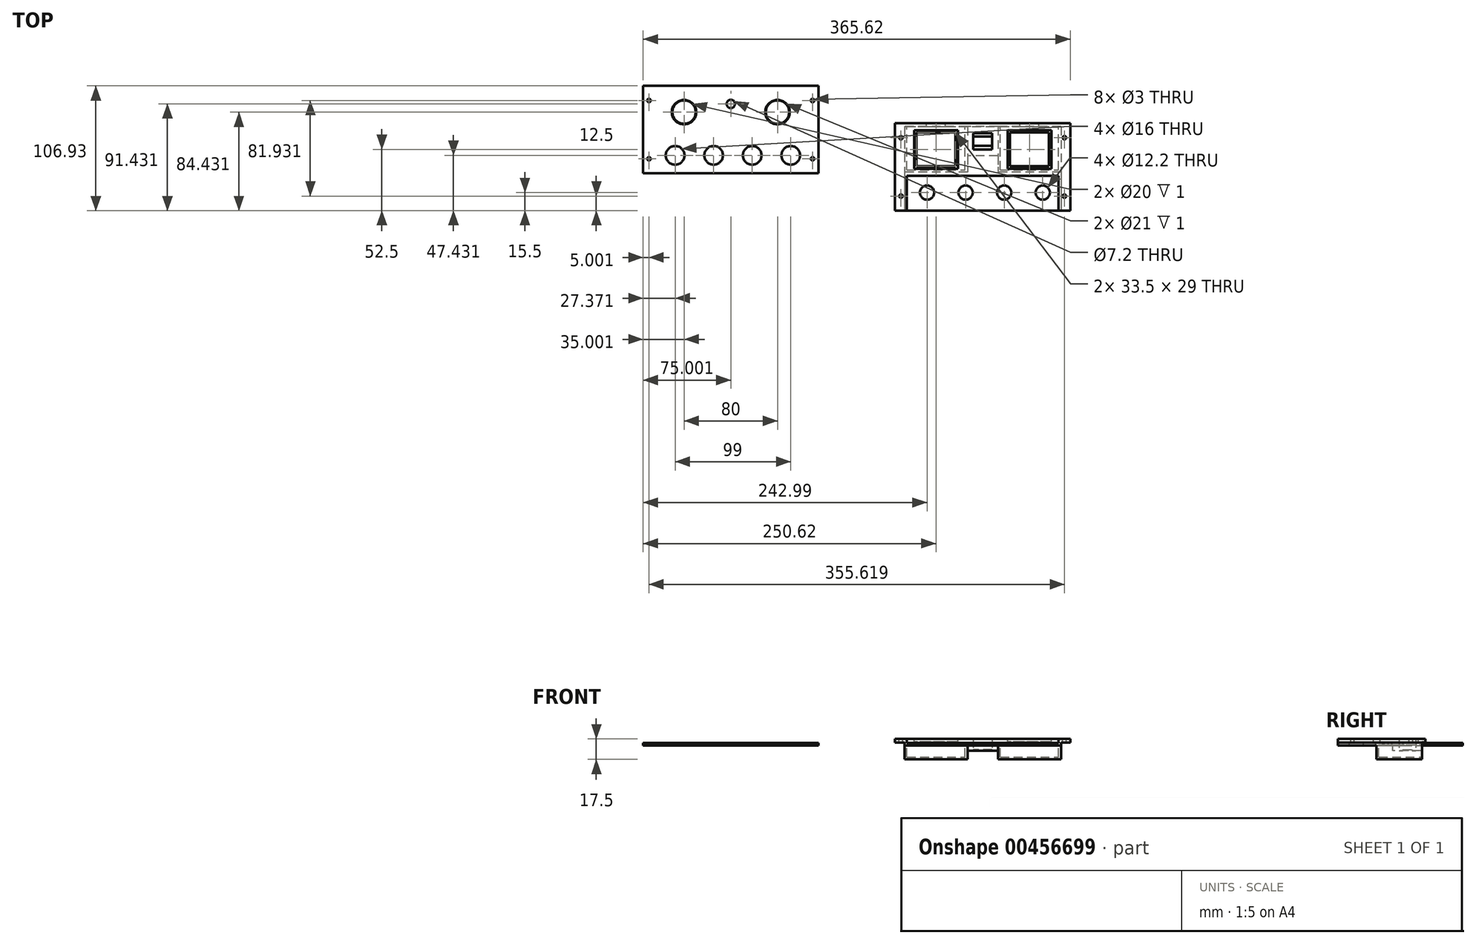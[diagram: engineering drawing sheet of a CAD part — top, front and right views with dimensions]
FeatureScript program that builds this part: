
annotation { "Feature Type Name" : "Feature", "Feature Type Description" : "" }
export const myFeature = defineFeature(function(context is Context, id is Id, definition is map)
    precondition{}
    {
        {
            var Q0;
            Q0=qCreatedBy(makeId("Top.planeOp"),FACE);
            var sketch = newSketch(context, id + "F0", { "sketchPlane" : qUnion([Q0])});
            skLineSegment(sketch, "E0.bottom", {"start": v(75, -37.5) * mm, "end": v(-75, -37.5) * mm});
            skLineSegment(sketch, "E0.top", {"start": v(75, 37.5) * mm, "end": v(-75, 37.5) * mm});
            skLineSegment(sketch, "E0.left", {"start": v(75, -37.5) * mm, "end": v(75, 37.5) * mm});
            skLineSegment(sketch, "E0.right", {"start": v(-75, -37.5) * mm, "end": v(-75, 37.5) * mm});
            skPoint(sketch, "E0.middle", {"position": v(0, 0) * mm});
            skCircle(sketch, "E1", {"center": v(0, 22) * mm, "radius": 5 * mm, "construction": true});
            skCircle(sketch, "E2", {"center": v(-47.63, -22) * mm, "radius": 6.1 * mm});
            skCircle(sketch, "E3.1.0.0", {"center": v(-14.63, -22) * mm, "radius": 6.1 * mm});
            skCircle(sketch, "E3.2.0.0", {"center": v(18.37, -22) * mm, "radius": 6.1 * mm});
            skCircle(sketch, "E3.3.0.0", {"center": v(51.37, -22) * mm, "radius": 6.1 * mm});
            skLineSegment(sketch, "E3.direction1", {"start": v(-47.63, -22) * mm, "end": v(-14.63, -22) * mm, "construction": true});
            skLineSegment(sketch, "E4.bottom", {"start": v(-75, 37.5) * mm, "end": v(-65, 37.5) * mm, "construction": true});
            skLineSegment(sketch, "E4.top", {"start": v(-75, -37.5) * mm, "end": v(-65, -37.5) * mm, "construction": true});
            skLineSegment(sketch, "E4.left", {"start": v(-75, 37.5) * mm, "end": v(-75, -37.5) * mm, "construction": true});
            skLineSegment(sketch, "E4.right", {"start": v(-65, 37.5) * mm, "end": v(-65, -37.5) * mm, "construction": true});
            skLineSegment(sketch, "E5.bottom", {"start": v(75, 37.5) * mm, "end": v(65, 37.5) * mm, "construction": true});
            skLineSegment(sketch, "E5.top", {"start": v(75, -37.5) * mm, "end": v(65, -37.5) * mm, "construction": true});
            skLineSegment(sketch, "E5.left", {"start": v(75, 37.5) * mm, "end": v(75, -37.5) * mm, "construction": true});
            skLineSegment(sketch, "E5.right", {"start": v(65, 37.5) * mm, "end": v(65, -37.5) * mm, "construction": true});
            skPoint(sketch, "E6.middle", {"position": v(-40, 15) * mm});
            skLineSegment(sketch, "E7.bottom", {"start": v(-23.25, 0.5) * mm, "end": v(-56.75, 0.5) * mm});
            skLineSegment(sketch, "E7.top", {"start": v(-23.25, 29.5) * mm, "end": v(-56.75, 29.5) * mm});
            skLineSegment(sketch, "E7.left", {"start": v(-23.25, 0.5) * mm, "end": v(-23.25, 29.5) * mm});
            skLineSegment(sketch, "E7.right", {"start": v(-56.75, 0.5) * mm, "end": v(-56.75, 29.5) * mm});
            skLineSegment(sketch, "E8.bottom", {"start": v(56.75, 0.5) * mm, "end": v(23.25, 0.5) * mm});
            skLineSegment(sketch, "E8.top", {"start": v(56.75, 29.5) * mm, "end": v(23.25, 29.5) * mm});
            skLineSegment(sketch, "E8.left", {"start": v(56.75, 0.5) * mm, "end": v(56.75, 29.5) * mm});
            skLineSegment(sketch, "E8.right", {"start": v(23.25, 0.5) * mm, "end": v(23.25, 29.5) * mm});
            skPoint(sketch, "E8.middle", {"position": v(40, 15) * mm});
            skPoint(sketch, "E9.centerSnap0", {"position": v(-70, 37.5) * mm});
            skCircle(sketch, "E10", {"center": v(-70, 25) * mm, "radius": 1.5 * mm});
            skCircle(sketch, "E11", {"center": v(-70, -25) * mm, "radius": 1.5 * mm});
            skCircle(sketch, "E12", {"center": v(70, 25) * mm, "radius": 1.5 * mm});
            skCircle(sketch, "E13", {"center": v(70, -25) * mm, "radius": 1.5 * mm});
            skLineSegment(sketch, "E14.bottom", {"start": v(8, 15) * mm, "end": v(-8, 15) * mm});
            skLineSegment(sketch, "E14.top", {"start": v(8, 29) * mm, "end": v(-8, 29) * mm});
            skLineSegment(sketch, "E14.left", {"start": v(8, 15) * mm, "end": v(8, 29) * mm});
            skLineSegment(sketch, "E14.right", {"start": v(-8, 15) * mm, "end": v(-8, 29) * mm});
            skLineSegment(sketch, "E15.bottom", {"start": v(8, 18) * mm, "end": v(-8, 18) * mm});
            skLineSegment(sketch, "E15.top", {"start": v(8, 26) * mm, "end": v(-8, 26) * mm});
            skLineSegment(sketch, "E15.left", {"start": v(8, 18) * mm, "end": v(8, 26) * mm});
            skLineSegment(sketch, "E15.right", {"start": v(-8, 18) * mm, "end": v(-8, 26) * mm});
            skSolve(sketch);
        }
        {
            var Q0;
            Q0=makeQuery(id+"F0.imprint","IMPRINT",FACE,{"disambiguationData":[TD([[makeQuery(id+"F0.imprint","IMPRINT",EDGE,{"derivedFrom":sQuery(id+"F0.wireOp",EDGE,"E0.bottom")}),-1.0]])]});
            var Q1;
            Q1=makeQuery(id+"F0.imprint","IMPRINT",FACE,{"disambiguationData":[TD([[makeQuery(id+"F0.imprint","IMPRINT",EDGE,{"derivedFrom":sQuery(id+"F0.wireOp",EDGE,"drD5jItb-HEpr-sxaA-TqkW-DfUxLCmm6Exs")}),-1.0]])]});
            var Q2;
            Q2=makeQuery(id+"F0.imprint","IMPRINT",FACE,{"disambiguationData":[TD([[makeQuery(id+"F0.imprint","IMPRINT",EDGE,{"derivedFrom":sQuery(id+"F0.wireOp",EDGE,"E15.bottom")}),-1.0]])]});
            extrude(context, id + "F1", {"entities" : qUnion([Q0, Q1, Q2]), "depth" : 2 * mm});
        }
        {
            var Q0;
            Q0=makeQuery(id+"F1.opExtrude","CAP_FACE",FACE,{"disambiguationData":[OSD([sQuery(id+"F0.wireOp",EDGE,"E0.bottom"),sQuery(id+"F0.wireOp",EDGE,"E0.top"),sQuery(id+"F0.wireOp",EDGE,"E0.left"),sQuery(id+"F0.wireOp",EDGE,"E0.right"),sQuery(id+"F0.wireOp",EDGE,"drD5jItb-HEpr-sxaA-TqkW-DfUxLCmm6Exs"),sQuery(id+"F0.wireOp",EDGE,"oSn99fef-1uPw-k3Do-L9e6-x1k65rtnndGm"),sQuery(id+"F0.wireOp",EDGE,"E1"),sQuery(id+"F0.wireOp",EDGE,"E2"),sQuery(id+"F0.wireOp",EDGE,"E3.1.0.0"),sQuery(id+"F0.wireOp",EDGE,"E3.2.0.0"),sQuery(id+"F0.wireOp",EDGE,"E3.3.0.0")])],"isStart":false});
            var sketch = newSketch(context, id + "F2", { "sketchPlane" : qUnion([Q0])});
            skLineSegment(sketch, "E16.bottom", {"start": v(-75, 37.5) * mm, "end": v(-65, 37.5) * mm});
            skLineSegment(sketch, "E16.top", {"start": v(-75, -37.5) * mm, "end": v(-65, -37.5) * mm});
            skLineSegment(sketch, "E16.left", {"start": v(-75, 37.5) * mm, "end": v(-75, -37.5) * mm});
            skLineSegment(sketch, "E16.right", {"start": v(-65, 37.5) * mm, "end": v(-65, -37.5) * mm});
            skLineSegment(sketch, "E17.bottom", {"start": v(75, -37.5) * mm, "end": v(65, -37.5) * mm});
            skLineSegment(sketch, "E17.top", {"start": v(75, 37.5) * mm, "end": v(65, 37.5) * mm});
            skLineSegment(sketch, "E17.left", {"start": v(75, -37.5) * mm, "end": v(75, 37.5) * mm});
            skLineSegment(sketch, "E17.right", {"start": v(65, -37.5) * mm, "end": v(65, 37.5) * mm});
            skSolve(sketch);
        }
        {
            var Q0;
            Q0=qSketchRegion(id+"F2",true);
            extrude(context, id + "F3", {"entities" : qUnion([Q0]), "operationType" : NewBodyOperationType.ADD, "depth" : 3.5 * mm});
        }
        {
            var Q0;
            Q0=makeQuery(id+"F3.boolean.opBoolean","MERGE",FACE,{"derivedFrom":[makeQuery(id+"F1.opExtrude","SWEPT_FACE",FACE,{"disambiguationData":[OSD([sQuery(id+"F0.wireOp",EDGE,"E0.bottom")])]}),makeQuery(id+"F3.opExtrude","SWEPT_FACE",FACE,{"disambiguationData":[OSD([sQuery(id+"F2.wireOp",EDGE,"E16.top")])]}),makeQuery(id+"F3.opExtrude","SWEPT_FACE",FACE,{"disambiguationData":[OSD([sQuery(id+"F2.wireOp",EDGE,"E17.bottom")])]})]});
            var sketch = newSketch(context, id + "F4", { "sketchPlane" : qUnion([Q0])});
            skLineSegment(sketch, "E18.bottom", {"start": v(-75, 0) * mm, "end": v(-67, 0) * mm});
            skLineSegment(sketch, "E18.top", {"start": v(-75, 2.5) * mm, "end": v(-67, 2.5) * mm});
            skLineSegment(sketch, "E18.left", {"start": v(-75, 0) * mm, "end": v(-75, 2.5) * mm});
            skLineSegment(sketch, "E18.right", {"start": v(-67, 0) * mm, "end": v(-67, 2.5) * mm});
            skLineSegment(sketch, "E19.bottom", {"start": v(75, 0) * mm, "end": v(67, 0) * mm});
            skLineSegment(sketch, "E19.top", {"start": v(75, 2.5) * mm, "end": v(67, 2.5) * mm});
            skLineSegment(sketch, "E19.left", {"start": v(75, 0) * mm, "end": v(75, 2.5) * mm});
            skLineSegment(sketch, "E19.right", {"start": v(67, 0) * mm, "end": v(67, 2.5) * mm});
            skSolve(sketch);
        }
        {
            var Q0;
            Q0=qSketchRegion(id+"F4",true);
            extrude(context, id + "F5", {"entities" : qUnion([Q0]), "operationType" : NewBodyOperationType.REMOVE, "oppositeDirection" : true, "depth" : 80 * mm});
        }
        {
            var Q0;
            Q0=makeQuery(id+"F1.opExtrude","CAP_FACE",FACE,{"disambiguationData":[OSD([sQuery(id+"F0.wireOp",EDGE,"E0.bottom"),sQuery(id+"F0.wireOp",EDGE,"E0.top"),sQuery(id+"F0.wireOp",EDGE,"E0.left"),sQuery(id+"F0.wireOp",EDGE,"E0.right"),sQuery(id+"F0.wireOp",EDGE,"drD5jItb-HEpr-sxaA-TqkW-DfUxLCmm6Exs"),sQuery(id+"F0.wireOp",EDGE,"oSn99fef-1uPw-k3Do-L9e6-x1k65rtnndGm"),sQuery(id+"F0.wireOp",EDGE,"E1"),sQuery(id+"F0.wireOp",EDGE,"E2"),sQuery(id+"F0.wireOp",EDGE,"E3.1.0.0"),sQuery(id+"F0.wireOp",EDGE,"E3.2.0.0"),sQuery(id+"F0.wireOp",EDGE,"E3.3.0.0")])],"isStart":false});
            var sketch = newSketch(context, id + "F6", { "sketchPlane" : qUnion([Q0])});
            skLineSegment(sketch, "E20.bottom", {"start": v(-65, 37.5) * mm, "end": v(65, 37.5) * mm});
            skLineSegment(sketch, "E20.top", {"start": v(-65, -7.5) * mm, "end": v(65, -7.5) * mm});
            skLineSegment(sketch, "E20.left", {"start": v(-65, 37.5) * mm, "end": v(-65, -7.5) * mm});
            skLineSegment(sketch, "E20.right", {"start": v(65, 37.5) * mm, "end": v(65, -7.5) * mm});
            skCircle(sketch, "E21", {"center": v(0, 22) * mm, "radius": 5 * mm, "construction": true});
            skLineSegment(sketch, "E22.bottom", {"start": v(-23.25, 0.5) * mm, "end": v(-56.75, 0.5) * mm});
            skLineSegment(sketch, "E22.top", {"start": v(-23.25, 29.5) * mm, "end": v(-56.75, 29.5) * mm});
            skLineSegment(sketch, "E22.left", {"start": v(-23.25, 0.5) * mm, "end": v(-23.25, 29.5) * mm});
            skLineSegment(sketch, "E22.right", {"start": v(-56.75, 0.5) * mm, "end": v(-56.75, 29.5) * mm});
            skPoint(sketch, "E22.middle", {"position": v(-40, 15) * mm});
            skLineSegment(sketch, "E23.bottom", {"start": v(56.75, 0.5) * mm, "end": v(23.25, 0.5) * mm});
            skLineSegment(sketch, "E23.top", {"start": v(56.75, 29.5) * mm, "end": v(23.25, 29.5) * mm});
            skLineSegment(sketch, "E23.left", {"start": v(56.75, 0.5) * mm, "end": v(56.75, 29.5) * mm});
            skLineSegment(sketch, "E23.right", {"start": v(23.25, 0.5) * mm, "end": v(23.25, 29.5) * mm});
            skPoint(sketch, "E23.middle", {"position": v(40, 15) * mm});
            skLineSegment(sketch, "E24.bottom", {"start": v(8, 15) * mm, "end": v(-8, 15) * mm});
            skLineSegment(sketch, "E24.top", {"start": v(8, 29) * mm, "end": v(-8, 29) * mm});
            skLineSegment(sketch, "E24.left", {"start": v(8, 15) * mm, "end": v(8, 29) * mm});
            skLineSegment(sketch, "E24.right", {"start": v(-8, 15) * mm, "end": v(-8, 29) * mm});
            skSolve(sketch);
        }
        {
            var Q0;
            Q0=qSketchRegion(id+"F6",true);
            extrude(context, id + "F7", {"entities" : qUnion([Q0]), "operationType" : NewBodyOperationType.ADD, "depth" : 3.5 * mm});
        }
        {
            var Q0;
            Q0=makeQuery(id+"F7.boolean.opBoolean","MERGE",FACE,{"derivedFrom":[makeQuery(id+"F3.opExtrude","CAP_FACE",FACE,{"disambiguationData":[OSD([sQuery(id+"F2.wireOp",EDGE,"E16.bottom"),sQuery(id+"F2.wireOp",EDGE,"E16.top"),sQuery(id+"F2.wireOp",EDGE,"E16.left"),sQuery(id+"F2.wireOp",EDGE,"E16.right")])],"isStart":false}),makeQuery(id+"F3.opExtrude","CAP_FACE",FACE,{"disambiguationData":[OSD([sQuery(id+"F2.wireOp",EDGE,"E17.bottom"),sQuery(id+"F2.wireOp",EDGE,"E17.top"),sQuery(id+"F2.wireOp",EDGE,"E17.left"),sQuery(id+"F2.wireOp",EDGE,"E17.right")])],"isStart":false}),makeQuery(id+"F7.opExtrude","CAP_FACE",FACE,{"disambiguationData":[OSD([sQuery(id+"F6.wireOp",EDGE,"E20.bottom"),sQuery(id+"F6.wireOp",EDGE,"E20.top"),sQuery(id+"F6.wireOp",EDGE,"E20.left"),sQuery(id+"F6.wireOp",EDGE,"E20.right"),sQuery(id+"F6.wireOp",EDGE,"H2Zb9yD0-p2Z7-Kh5e-a6hj-aLUdcpXocAIw"),sQuery(id+"F6.wireOp",EDGE,"7ZJ2aJG6-LJXW-fwXF-v4kC-qdLRGwjfnqPK"),sQuery(id+"F6.wireOp",EDGE,"E21")])],"isStart":false})]});
            var sketch = newSketch(context, id + "F8", { "sketchPlane" : qUnion([Q0])});
            skLineSegment(sketch, "E25.bottom", {"start": v(-21.25, -1.5) * mm, "end": v(-58.75, -1.5) * mm});
            skLineSegment(sketch, "E25.top", {"start": v(-21.25, 31.5) * mm, "end": v(-58.75, 31.5) * mm});
            skLineSegment(sketch, "E25.left", {"start": v(-21.25, -1.5) * mm, "end": v(-21.25, 31.5) * mm});
            skLineSegment(sketch, "E25.right", {"start": v(-58.75, -1.5) * mm, "end": v(-58.75, 31.5) * mm});
            skPoint(sketch, "E25.middle", {"position": v(-40, 15) * mm});
            skLineSegment(sketch, "E26.bottom", {"start": v(58.75, -1.5) * mm, "end": v(21.25, -1.5) * mm});
            skLineSegment(sketch, "E26.top", {"start": v(58.75, 31.5) * mm, "end": v(21.25, 31.5) * mm});
            skLineSegment(sketch, "E26.left", {"start": v(58.75, -1.5) * mm, "end": v(58.75, 31.5) * mm});
            skLineSegment(sketch, "E26.right", {"start": v(21.25, -1.5) * mm, "end": v(21.25, 31.5) * mm});
            skPoint(sketch, "E26.middle", {"position": v(40, 15) * mm});
            skLineSegment(sketch, "E27.bottom", {"start": v(-32, 31.5) * mm, "end": v(-48, 31.5) * mm});
            skLineSegment(sketch, "E27.top", {"start": v(-32, 46.5) * mm, "end": v(-48, 46.5) * mm});
            skLineSegment(sketch, "E27.left", {"start": v(-32, 31.5) * mm, "end": v(-32, 46.5) * mm});
            skLineSegment(sketch, "E27.right", {"start": v(-48, 31.5) * mm, "end": v(-48, 46.5) * mm});
            skPoint(sketch, "E27.middle", {"position": v(-40, 39) * mm});
            skPoint(sketch, "E27.middle.positionSnap0", {"position": v(-40, 31.5) * mm});
            skPoint(sketch, "E27.centerSnap0", {"position": v(-40, 31.5) * mm});
            skLineSegment(sketch, "E28.bottom", {"start": v(48, 31.5) * mm, "end": v(32, 31.5) * mm});
            skLineSegment(sketch, "E28.top", {"start": v(48, 46.5) * mm, "end": v(32, 46.5) * mm});
            skLineSegment(sketch, "E28.left", {"start": v(48, 31.5) * mm, "end": v(48, 46.5) * mm});
            skLineSegment(sketch, "E28.right", {"start": v(32, 31.5) * mm, "end": v(32, 46.5) * mm});
            skPoint(sketch, "E28.middle", {"position": v(40, 39) * mm});
            skPoint(sketch, "E28.middle.positionSnap0", {"position": v(40, 31.5) * mm});
            skPoint(sketch, "E28.centerSnap0", {"position": v(40, 31.5) * mm});
            skSolve(sketch);
        }
        {
            var Q0;
            Q0=makeQuery(id+"F8.imprint","IMPRINT",FACE,{"disambiguationData":[TD([[makeQuery(id+"F8.imprint","IMPRINT",EDGE,{"derivedFrom":sQuery(id+"F8.wireOp",EDGE,"E25.bottom")}),-1.0]])]});
            var Q1;
            Q1=makeQuery(id+"F8.imprint","IMPRINT",FACE,{"disambiguationData":[TD([[makeQuery(id+"F8.imprint","IMPRINT",EDGE,{"derivedFrom":sQuery(id+"F8.wireOp",EDGE,"E26.bottom")}),-1.0]])]});
            var Q2;
            {var subQ0=sQuery(id+"F8.wireOp",EDGE,"E27.top");Q2=makeQuery(id+"F8.imprint","IMPRINT",FACE,{"disambiguationData":[TD([[makeQuery(id+"F8.imprint","IMPRINT",EDGE,{"derivedFrom":subQ0}),1.0]])]});}
            var Q3;
            {var subQ0=sQuery(id+"F8.wireOp",EDGE,"E28.top");Q3=makeQuery(id+"F8.imprint","IMPRINT",FACE,{"disambiguationData":[TD([[makeQuery(id+"F8.imprint","IMPRINT",EDGE,{"derivedFrom":subQ0}),1.0]])]});}
            var Q4;
            {var subQ0=sQuery(id+"F8.wireOp",EDGE,"E27.bottom");Q4=makeQuery(id+"F8.imprint","IMPRINT",FACE,{"disambiguationData":[TD([[makeQuery(id+"F8.imprint","IMPRINT",EDGE,{"derivedFrom":subQ0}),-1.0]])]});}
            var Q5;
            {var subQ0=sQuery(id+"F8.wireOp",EDGE,"E28.bottom");Q5=makeQuery(id+"F8.imprint","IMPRINT",FACE,{"disambiguationData":[TD([[makeQuery(id+"F8.imprint","IMPRINT",EDGE,{"derivedFrom":subQ0}),-1.0]])]});}
            extrude(context, id + "F9", {"entities" : qUnion([Q0, Q1, Q2, Q3, Q4, Q5]), "operationType" : NewBodyOperationType.REMOVE, "oppositeDirection" : true, "depth" : 2.5 * mm});
        }
        {
            var Q0;
            Q0=qCreatedBy(makeId("Top.planeOp"),FACE);
            var sketch = newSketch(context, id + "F10", { "sketchPlane" : qUnion([Q0])});
            skLineSegment(sketch, "E29.bottom", {"start": v(-140.62, -5.57) * mm, "end": v(-290.62, -5.57) * mm});
            skLineSegment(sketch, "E29.top", {"start": v(-140.62, 69.43) * mm, "end": v(-290.62, 69.43) * mm});
            skLineSegment(sketch, "E29.left", {"start": v(-140.62, -5.57) * mm, "end": v(-140.62, 69.43) * mm});
            skLineSegment(sketch, "E29.right", {"start": v(-290.62, -5.57) * mm, "end": v(-290.62, 69.43) * mm});
            skPoint(sketch, "E29.middle", {"position": v(-215.62, 31.93) * mm});
            skCircle(sketch, "E30", {"center": v(-215.62, 53.93) * mm, "radius": 3.6 * mm});
            skCircle(sketch, "E31", {"center": v(-263.25, 9.93) * mm, "radius": 8 * mm});
            skCircle(sketch, "E32.1.0.0", {"center": v(-230.25, 9.93) * mm, "radius": 8 * mm});
            skCircle(sketch, "E32.2.0.0", {"center": v(-197.25, 9.93) * mm, "radius": 8 * mm});
            skCircle(sketch, "E32.3.0.0", {"center": v(-164.25, 9.93) * mm, "radius": 8 * mm});
            skLineSegment(sketch, "E32.direction1", {"start": v(-263.25, 9.93) * mm, "end": v(-230.25, 9.93) * mm, "construction": true});
            skLineSegment(sketch, "E33.bottom", {"start": v(-290.62, 69.43) * mm, "end": v(-280.62, 69.43) * mm, "construction": true});
            skLineSegment(sketch, "E33.top", {"start": v(-290.62, -5.57) * mm, "end": v(-280.62, -5.57) * mm, "construction": true});
            skLineSegment(sketch, "E33.left", {"start": v(-290.62, 69.43) * mm, "end": v(-290.62, -5.57) * mm, "construction": true});
            skLineSegment(sketch, "E33.right", {"start": v(-280.62, 69.43) * mm, "end": v(-280.62, -5.57) * mm, "construction": true});
            skLineSegment(sketch, "E34.bottom", {"start": v(-140.62, 69.43) * mm, "end": v(-150.62, 69.43) * mm, "construction": true});
            skLineSegment(sketch, "E34.top", {"start": v(-140.62, -5.57) * mm, "end": v(-150.62, -5.57) * mm, "construction": true});
            skLineSegment(sketch, "E34.left", {"start": v(-140.62, 69.43) * mm, "end": v(-140.62, -5.57) * mm, "construction": true});
            skLineSegment(sketch, "E34.right", {"start": v(-150.62, 69.43) * mm, "end": v(-150.62, -5.57) * mm, "construction": true});
            skPoint(sketch, "E35.middle", {"position": v(-255.62, 46.93) * mm});
            skPoint(sketch, "E36.middle", {"position": v(-175.62, 46.93) * mm});
            skCircle(sketch, "E37", {"center": v(-255.62, 46.93) * mm, "radius": 10 * mm});
            skCircle(sketch, "E38", {"center": v(-175.62, 46.93) * mm, "radius": 10 * mm});
            skLineSegment(sketch, "E39.bottom", {"start": v(-236.87, 30.43) * mm, "end": v(-274.37, 30.43) * mm, "construction": true});
            skLineSegment(sketch, "E39.top", {"start": v(-236.87, 63.43) * mm, "end": v(-274.37, 63.43) * mm, "construction": true});
            skLineSegment(sketch, "E39.left", {"start": v(-236.87, 30.43) * mm, "end": v(-236.87, 63.43) * mm, "construction": true});
            skLineSegment(sketch, "E39.right", {"start": v(-274.37, 30.43) * mm, "end": v(-274.37, 63.43) * mm, "construction": true});
            skLineSegment(sketch, "E40.bottom", {"start": v(-156.87, 30.43) * mm, "end": v(-194.37, 30.43) * mm, "construction": true});
            skLineSegment(sketch, "E40.top", {"start": v(-156.87, 63.43) * mm, "end": v(-194.37, 63.43) * mm, "construction": true});
            skLineSegment(sketch, "E40.left", {"start": v(-156.87, 30.43) * mm, "end": v(-156.87, 63.43) * mm, "construction": true});
            skLineSegment(sketch, "E40.right", {"start": v(-194.37, 30.43) * mm, "end": v(-194.37, 63.43) * mm, "construction": true});
            skCircle(sketch, "E41", {"center": v(-285.62, 56.93) * mm, "radius": 1.5 * mm});
            skCircle(sketch, "E42", {"center": v(-285.62, 6.93) * mm, "radius": 1.5 * mm});
            skCircle(sketch, "E43", {"center": v(-145.62, 56.93) * mm, "radius": 1.5 * mm});
            skCircle(sketch, "E44", {"center": v(-145.62, 6.93) * mm, "radius": 1.5 * mm});
            skSolve(sketch);
        }
        {
            var Q0;
            Q0=makeQuery(id+"F10.imprint","IMPRINT",FACE,{"disambiguationData":[TD([[makeQuery(id+"F10.imprint","IMPRINT",EDGE,{"derivedFrom":sQuery(id+"F10.wireOp",EDGE,"E29.bottom")}),-1.0]])]});
            extrude(context, id + "F11", {"entities" : qUnion([Q0]), "depth" : 2 * mm});
        }
        {
            var Q0;
            Q0=makeQuery(id+"F11.opExtrude","CAP_FACE",FACE,{"disambiguationData":[OSD([sQuery(id+"F10.wireOp",EDGE,"E29.bottom"),sQuery(id+"F10.wireOp",EDGE,"E29.top"),sQuery(id+"F10.wireOp",EDGE,"E29.left"),sQuery(id+"F10.wireOp",EDGE,"E29.right"),sQuery(id+"F10.wireOp",EDGE,"E30"),sQuery(id+"F10.wireOp",EDGE,"E31"),sQuery(id+"F10.wireOp",EDGE,"E32.1.0.0"),sQuery(id+"F10.wireOp",EDGE,"E32.2.0.0"),sQuery(id+"F10.wireOp",EDGE,"E32.3.0.0"),sQuery(id+"F10.wireOp",EDGE,"E37"),sQuery(id+"F10.wireOp",EDGE,"E38")])],"isStart":false});
            var sketch = newSketch(context, id + "F12", { "sketchPlane" : qUnion([Q0])});
            skLineSegment(sketch, "E45.bottom", {"start": v(-239.12, 65.68) * mm, "end": v(-272.12, 65.68) * mm, "construction": true});
            skLineSegment(sketch, "E45.top", {"start": v(-239.12, 28.18) * mm, "end": v(-272.12, 28.18) * mm, "construction": true});
            skLineSegment(sketch, "E45.left", {"start": v(-239.12, 65.68) * mm, "end": v(-239.12, 28.18) * mm, "construction": true});
            skLineSegment(sketch, "E45.right", {"start": v(-272.12, 65.68) * mm, "end": v(-272.12, 28.18) * mm, "construction": true});
            skPoint(sketch, "E45.middle", {"position": v(-255.62, 46.93) * mm});
            skLineSegment(sketch, "E46.bottom", {"start": v(-159.12, 65.68) * mm, "end": v(-192.12, 65.68) * mm, "construction": true});
            skLineSegment(sketch, "E46.top", {"start": v(-159.12, 28.18) * mm, "end": v(-192.12, 28.18) * mm, "construction": true});
            skLineSegment(sketch, "E46.left", {"start": v(-159.12, 65.68) * mm, "end": v(-159.12, 28.18) * mm, "construction": true});
            skLineSegment(sketch, "E46.right", {"start": v(-192.12, 65.68) * mm, "end": v(-192.12, 28.18) * mm, "construction": true});
            skPoint(sketch, "E46.middle", {"position": v(-175.62, 46.93) * mm});
            skCircle(sketch, "E47", {"center": v(-255.62, 46.93) * mm, "radius": 10.5 * mm});
            skCircle(sketch, "E48", {"center": v(-175.62, 46.93) * mm, "radius": 10.5 * mm});
            skSolve(sketch);
        }
        {
            var Q0;
            Q0=qSketchRegion(id+"F12",true);
            extrude(context, id + "F13", {"entities" : qUnion([Q0]), "operationType" : NewBodyOperationType.REMOVE, "oppositeDirection" : true, "depth" : 1 * mm});
        }
        {
            var Q0;
            Q0=makeQuery(id+"F0.imprint","IMPRINT",FACE,{"disambiguationData":[TD([[makeQuery(id+"F0.imprint","IMPRINT",EDGE,{"derivedFrom":sQuery(id+"F0.wireOp",EDGE,"E0.bottom")}),-1.0]])]});
            var sketch = newSketch(context, id + "F14", { "sketchPlane" : qUnion([Q0])});
            skPoint(sketch, "E49.0", {"position": v(0, 22) * mm});
            skLineSegment(sketch, "E50.bottom", {"start": v(13, 34.5) * mm, "end": v(-13, 34.5) * mm});
            skLineSegment(sketch, "E50.top", {"start": v(13, 9.5) * mm, "end": v(-13, 9.5) * mm});
            skLineSegment(sketch, "E50.left", {"start": v(13, 34.5) * mm, "end": v(13, 9.5) * mm});
            skLineSegment(sketch, "E50.right", {"start": v(-13, 34.5) * mm, "end": v(-13, 9.5) * mm});
            skPoint(sketch, "E51.0", {"position": v(8, 26) * mm});
            skLineSegment(sketch, "E52.bottom", {"start": v(8, 26) * mm, "end": v(-8, 26) * mm});
            skLineSegment(sketch, "E52.top", {"start": v(8, 18) * mm, "end": v(-8, 18) * mm});
            skLineSegment(sketch, "E52.left", {"start": v(8, 26) * mm, "end": v(8, 18) * mm});
            skLineSegment(sketch, "E52.right", {"start": v(-8, 26) * mm, "end": v(-8, 18) * mm});
            skSolve(sketch);
        }
        {
            var Q0;
            Q0=makeQuery(id+"F14.imprint","IMPRINT",FACE,{"disambiguationData":[TD([[makeQuery(id+"F14.imprint","IMPRINT",EDGE,{"derivedFrom":sQuery(id+"F14.wireOp",EDGE,"E50.bottom")}),1.0]])]});
            var Q1;
            Q1=makeQuery(id+"F0.imprint","IMPRINT",FACE,{"disambiguationData":[TD([[makeQuery(id+"F0.imprint","IMPRINT",EDGE,{"derivedFrom":sQuery(id+"F0.wireOp",EDGE,"E15.bottom")}),-1.0]])]});
            extrude(context, id + "F15", {"entities" : qUnion([Q0, Q1]), "operationType" : NewBodyOperationType.ADD, "oppositeDirection" : true, "depth" : 4.5 * mm});
        }
        {
            var Q0;
            Q0=makeQuery(id+"F7.boolean.opBoolean","MERGE",FACE,{"derivedFrom":[makeQuery(id+"F3.opExtrude","CAP_FACE",FACE,{"disambiguationData":[OSD([sQuery(id+"F2.wireOp",EDGE,"E16.bottom"),sQuery(id+"F2.wireOp",EDGE,"E16.top"),sQuery(id+"F2.wireOp",EDGE,"E16.left"),sQuery(id+"F2.wireOp",EDGE,"E16.right")])],"isStart":false}),makeQuery(id+"F3.opExtrude","CAP_FACE",FACE,{"disambiguationData":[OSD([sQuery(id+"F2.wireOp",EDGE,"E17.bottom"),sQuery(id+"F2.wireOp",EDGE,"E17.top"),sQuery(id+"F2.wireOp",EDGE,"E17.left"),sQuery(id+"F2.wireOp",EDGE,"E17.right")])],"isStart":false}),makeQuery(id+"F7.opExtrude","CAP_FACE",FACE,{"disambiguationData":[OSD([sQuery(id+"F6.wireOp",EDGE,"E20.bottom"),sQuery(id+"F6.wireOp",EDGE,"E20.top"),sQuery(id+"F6.wireOp",EDGE,"E20.left"),sQuery(id+"F6.wireOp",EDGE,"E20.right"),sQuery(id+"F6.wireOp",EDGE,"E22.bottom"),sQuery(id+"F6.wireOp",EDGE,"E22.top"),sQuery(id+"F6.wireOp",EDGE,"E22.left"),sQuery(id+"F6.wireOp",EDGE,"E22.right"),sQuery(id+"F6.wireOp",EDGE,"E23.bottom"),sQuery(id+"F6.wireOp",EDGE,"E23.top"),sQuery(id+"F6.wireOp",EDGE,"E23.left"),sQuery(id+"F6.wireOp",EDGE,"E23.right"),sQuery(id+"F6.wireOp",EDGE,"E24.bottom"),sQuery(id+"F6.wireOp",EDGE,"E24.top"),sQuery(id+"F6.wireOp",EDGE,"E24.left"),sQuery(id+"F6.wireOp",EDGE,"E24.right")])],"isStart":false})]});
            var sketch = newSketch(context, id + "F16", { "sketchPlane" : qUnion([Q0])});
            skPoint(sketch, "E53.0", {"position": v(0, 22) * mm});
            skLineSegment(sketch, "E54.bottom", {"start": v(8, 15) * mm, "end": v(-8, 15) * mm});
            skLineSegment(sketch, "E54.top", {"start": v(8, 29) * mm, "end": v(-8, 29) * mm});
            skLineSegment(sketch, "E54.left", {"start": v(8, 15) * mm, "end": v(8, 29) * mm});
            skLineSegment(sketch, "E54.right", {"start": v(-8, 15) * mm, "end": v(-8, 29) * mm});
            skSolve(sketch);
        }
        {
            var Q0;
            Q0=qSketchRegion(id+"F16",true);
            extrude(context, id + "F17", {"entities" : qUnion([Q0]), "operationType" : NewBodyOperationType.REMOVE, "oppositeDirection" : true, "depth" : 9 * mm});
        }
        {
            var Q0;
            Q0=makeQuery(id+"F0.imprint","IMPRINT",FACE,{"disambiguationData":[TD([[makeQuery(id+"F0.imprint","IMPRINT",EDGE,{"derivedFrom":sQuery(id+"F0.wireOp",EDGE,"E0.bottom")}),-1.0]])]});
            var sketch = newSketch(context, id + "F18", { "sketchPlane" : qUnion([Q0])});
            skPoint(sketch, "E55.0", {"position": v(-67, 37.5) * mm});
            skPoint(sketch, "E55.1", {"position": v(67, 37.5) * mm});
            skLineSegment(sketch, "E56.bottom", {"start": v(-67, 37.5) * mm, "end": v(67, 37.5) * mm});
            skLineSegment(sketch, "E56.top", {"start": v(-67, 34.5) * mm, "end": v(67, 34.5) * mm});
            skLineSegment(sketch, "E56.left", {"start": v(-67, 37.5) * mm, "end": v(-67, 34.5) * mm});
            skLineSegment(sketch, "E56.right", {"start": v(67, 37.5) * mm, "end": v(67, 34.5) * mm});
            skSolve(sketch);
        }
        {
            var Q0;
            Q0=makeQuery(id+"F18.imprint","IMPRINT",FACE,{"disambiguationData":[TD([[makeQuery(id+"F18.imprint","IMPRINT",EDGE,{"derivedFrom":sQuery(id+"F18.wireOp",EDGE,"E56.bottom")}),1.0]])]});
            extrude(context, id + "F19", {"entities" : qUnion([Q0]), "operationType" : NewBodyOperationType.REMOVE, "depth" : 2.5 * mm});
        }
        {
            var Q0;
            Q0=makeQuery(id+"F0.imprint","IMPRINT",FACE,{"disambiguationData":[TD([[makeQuery(id+"F0.imprint","IMPRINT",EDGE,{"derivedFrom":sQuery(id+"F0.wireOp",EDGE,"E0.bottom")}),-1.0]])]});
            var sketch = newSketch(context, id + "F20", { "sketchPlane" : qUnion([Q0])});
            skPoint(sketch, "E57.0", {"position": v(-40, 15) * mm});
            skPoint(sketch, "E57.1", {"position": v(40, 15) * mm});
            skLineSegment(sketch, "E58.bottom", {"start": v(-13, 34.5) * mm, "end": v(-67, 34.5) * mm});
            skLineSegment(sketch, "E58.top", {"start": v(-13, -4.5) * mm, "end": v(-67, -4.5) * mm});
            skLineSegment(sketch, "E58.left", {"start": v(-13, 34.5) * mm, "end": v(-13, -4.5) * mm});
            skLineSegment(sketch, "E58.right", {"start": v(-67, 34.5) * mm, "end": v(-67, -4.5) * mm});
            skLineSegment(sketch, "E59.bottom", {"start": v(67, 34.5) * mm, "end": v(13, 34.5) * mm});
            skLineSegment(sketch, "E59.top", {"start": v(67, -4.5) * mm, "end": v(13, -4.5) * mm});
            skLineSegment(sketch, "E59.left", {"start": v(67, 34.5) * mm, "end": v(67, -4.5) * mm});
            skLineSegment(sketch, "E59.right", {"start": v(13, 34.5) * mm, "end": v(13, -4.5) * mm});
            skSolve(sketch);
        }
        {
            var Q0;
            Q0=makeQuery(id+"F20.imprint","IMPRINT",FACE,{"disambiguationData":[TD([[makeQuery(id+"F20.imprint","IMPRINT",EDGE,{"derivedFrom":sQuery(id+"F20.wireOp",EDGE,"E59.bottom")}),1.0]])]});
            var Q1;
            Q1=makeQuery(id+"F20.imprint","IMPRINT",FACE,{"disambiguationData":[TD([[makeQuery(id+"F20.imprint","IMPRINT",EDGE,{"derivedFrom":sQuery(id+"F20.wireOp",EDGE,"E58.bottom")}),1.0]])]});
            var Q2;
            Q2=makeQuery(id+"F20.imprint","IMPRINT",FACE,{"disambiguationData":[TD([[makeQuery(id+"F20.imprint","IMPRINT",EDGE,{"derivedFrom":makeQuery(id+"F0.imprint","IMPRINT",EDGE,{"derivedFrom":sQuery(id+"F0.wireOp",EDGE,"E8.bottom")})}),-1.0]])]});
            var Q3;
            Q3=makeQuery(id+"F20.imprint","IMPRINT",FACE,{"disambiguationData":[TD([[makeQuery(id+"F20.imprint","IMPRINT",EDGE,{"derivedFrom":makeQuery(id+"F0.imprint","IMPRINT",EDGE,{"derivedFrom":sQuery(id+"F0.wireOp",EDGE,"E7.bottom")})}),-1.0]])]});
            extrude(context, id + "F21", {"entities" : qUnion([Q0, Q1, Q2, Q3]), "operationType" : NewBodyOperationType.ADD, "oppositeDirection" : true, "depth" : 12 * mm});
        }
        {
            var Q0;
            Q0=makeQuery(id+"F21.boolean.opBoolean","MERGE",FACE,{"derivedFrom":[makeQuery(id+"F19.boolean.opBoolean","MERGE",FACE,{"derivedFrom":[makeQuery(id+"F15.opExtrude","SWEPT_FACE",FACE,{"disambiguationData":[OSD([sQuery(id+"F14.wireOp",EDGE,"E50.bottom")])]}),makeQuery(id+"F19.opExtrude","SWEPT_FACE",FACE,{"disambiguationData":[OSD([sQuery(id+"F18.wireOp",EDGE,"E56.top")])]})]}),makeQuery(id+"F21.opExtrude","SWEPT_FACE",FACE,{"disambiguationData":[OSD([sQuery(id+"F20.wireOp",EDGE,"E58.bottom")])]}),makeQuery(id+"F21.opExtrude","SWEPT_FACE",FACE,{"disambiguationData":[OSD([sQuery(id+"F20.wireOp",EDGE,"E59.bottom")])]})]});
            var sketch = newSketch(context, id + "F22", { "sketchPlane" : qUnion([Q0])});
            skLineSegment(sketch, "E60.bottom", {"start": v(-15, -10) * mm, "end": v(-65, -10) * mm});
            skLineSegment(sketch, "E60.top", {"start": v(-15, 0.5) * mm, "end": v(-65, 0.5) * mm});
            skLineSegment(sketch, "E60.left", {"start": v(-15, -10) * mm, "end": v(-15, 0.5) * mm});
            skLineSegment(sketch, "E60.right", {"start": v(-65, -10) * mm, "end": v(-65, 0.5) * mm});
            skPoint(sketch, "E60.middle", {"position": v(-40, -4.75) * mm});
            skPoint(sketch, "E60.middle.positionSnap0", {"position": v(-40, -12) * mm});
            skPoint(sketch, "E60.middle.positionSnap1", {"position": v(-67, -4.75) * mm});
            skPoint(sketch, "E60.centerSnap0", {"position": v(-40, -12) * mm});
            skPoint(sketch, "E60.centerSnap1", {"position": v(-67, -4.75) * mm});
            skLineSegment(sketch, "E61.bottom", {"start": v(65, -10) * mm, "end": v(15, -10) * mm});
            skLineSegment(sketch, "E61.top", {"start": v(65, 0.5) * mm, "end": v(15, 0.5) * mm});
            skLineSegment(sketch, "E61.left", {"start": v(65, -10) * mm, "end": v(65, 0.5) * mm});
            skLineSegment(sketch, "E61.right", {"start": v(15, -10) * mm, "end": v(15, 0.5) * mm});
            skPoint(sketch, "E61.middle", {"position": v(40, -4.75) * mm});
            skPoint(sketch, "E61.middle.positionSnap0", {"position": v(40, -12) * mm});
            skPoint(sketch, "E61.middle.positionSnap1", {"position": v(67, -4.75) * mm});
            skPoint(sketch, "E61.centerSnap0", {"position": v(40, -12) * mm});
            skPoint(sketch, "E61.centerSnap1", {"position": v(67, -4.75) * mm});
            skSolve(sketch);
        }
        {
            var Q0;
            Q0=qSketchRegion(id+"F22",true);
            extrude(context, id + "F23", {"entities" : qUnion([Q0]), "operationType" : NewBodyOperationType.REMOVE, "oppositeDirection" : true, "depth" : 37 * mm});
        }
        {
            var Q0;
            Q0=makeQuery(id+"F16.imprint","IMPRINT",FACE,{"disambiguationData":[TD([[makeQuery(id+"F16.imprint","IMPRINT",EDGE,{"derivedFrom":sQuery(id+"F16.wireOp",EDGE,"E54.bottom")}),1.0]])]});
            var sketch = newSketch(context, id + "F24", { "sketchPlane" : qUnion([Q0])});
            skPoint(sketch, "E62.0", {"position": v(-70, 25) * mm});
            skPoint(sketch, "E62.1", {"position": v(-70, -25) * mm});
            skPoint(sketch, "E62.2", {"position": v(70, -25) * mm});
            skPoint(sketch, "E62.3", {"position": v(70, 25) * mm});
            skCircle(sketch, "E63", {"center": v(-70, 25) * mm, "radius": 1.5 * mm});
            skCircle(sketch, "E64", {"center": v(-70, -25) * mm, "radius": 1.5 * mm});
            skCircle(sketch, "E65", {"center": v(70, 25) * mm, "radius": 1.5 * mm});
            skCircle(sketch, "E66", {"center": v(70, -25) * mm, "radius": 1.5 * mm});
            skSolve(sketch);
        }
        {
            var Q0;
            Q0=qSketchRegion(id+"F24",true);
            extrude(context, id + "F25", {"entities" : qUnion([Q0]), "operationType" : NewBodyOperationType.REMOVE, "oppositeDirection" : true, "depth" : 25 * mm});
        }
        {
            var Q0;
            Q0=makeQuery(id+"F9.boolean.opBoolean","COPY",FACE,{"derivedFrom":makeQuery(id+"F9.opExtrude","CAP_FACE",FACE,{"disambiguationData":[OSD([sQuery(id+"F6.wireOp",EDGE,"E22.bottom"),sQuery(id+"F6.wireOp",EDGE,"E22.top"),sQuery(id+"F6.wireOp",EDGE,"E22.left"),sQuery(id+"F6.wireOp",EDGE,"E22.right"),sQuery(id+"F8.wireOp",EDGE,"E25.bottom"),sQuery(id+"F8.wireOp",EDGE,"E25.top"),sQuery(id+"F8.wireOp",EDGE,"E25.left"),sQuery(id+"F8.wireOp",EDGE,"E25.right"),sQuery(id+"F8.wireOp",EDGE,"E27.top"),sQuery(id+"F8.wireOp",EDGE,"E27.left"),sQuery(id+"F8.wireOp",EDGE,"E27.right")])],"isStart":false})});
            var sketch = newSketch(context, id + "F26", { "sketchPlane" : qUnion([Q0])});
            skLineSegment(sketch, "E67.bottom", {"start": v(-48, 37.5) * mm, "end": v(-32, 37.5) * mm});
            skLineSegment(sketch, "E67.top", {"start": v(-48, 34.5) * mm, "end": v(-32, 34.5) * mm});
            skLineSegment(sketch, "E67.left", {"start": v(-48, 37.5) * mm, "end": v(-48, 34.5) * mm});
            skLineSegment(sketch, "E67.right", {"start": v(-32, 37.5) * mm, "end": v(-32, 34.5) * mm});
            skLineSegment(sketch, "E68.bottom", {"start": v(32, 37.5) * mm, "end": v(48, 37.5) * mm});
            skLineSegment(sketch, "E68.top", {"start": v(32, 34.5) * mm, "end": v(48, 34.5) * mm});
            skLineSegment(sketch, "E68.left", {"start": v(32, 37.5) * mm, "end": v(32, 34.5) * mm});
            skLineSegment(sketch, "E68.right", {"start": v(48, 37.5) * mm, "end": v(48, 34.5) * mm});
            skSolve(sketch);
        }
        {
            var Q0;
            Q0=qSketchRegion(id+"F26",true);
            extrude(context, id + "F27", {"entities" : qUnion([Q0]), "operationType" : NewBodyOperationType.REMOVE, "oppositeDirection" : true, "depth" : 3 * mm});
        }
    });
